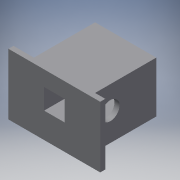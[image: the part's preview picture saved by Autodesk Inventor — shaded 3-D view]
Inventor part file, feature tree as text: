
AUTODESK INVENTOR PART (.ipt)
format: ipt  version: 2016 (Build 200138000, 138)  size: 137,728 bytes
history: native  units: mm
features: extrude x5, sketch x5
ambient origin geometry x8: Origin, YZ Plane, XZ Plane, XY Plane, X Axis, Y Axis, Z Axis, Center Point
bodies: Solid1 (feature_tree)
feature tree (10):
  extrude  "Extrusion1"  Depth=10.0mm
  extrude  "Extrusion2"  Depth=13.0mm
  extrude  "Extrusion3"  Depth=4.0mm
  extrude  "Extrusion4"  Depth=13.0mm TaperAngle=0.0deg
  extrude  "Extrusion5"  Depth=1.0mm
  sketch  "Sketch1"  dims[d0=12.0mm d1=10.0mm]
  sketch  "Sketch2"  dims[d2=13.0mm d3=0.0mm d4=3.6mm]
  sketch  "Sketch3"  dims[d5=4.0mm d7=5.5mm]
  sketch  "Sketch4"  dims[d8=4.5mm d9=13.0mm d10=0.0mm]
  sketch  "Sketch5"  dims[d11=1.0mm d12=1.0mm d14=1.0mm d15=1.0mm d16=13.0mm d17=0.0mm d18=3.0mm d19=3.0mm d20=1.0mm d21=1.0mm d22=1.0mm d23=0.0mm d27=2.0mm d28=4.0mm d29=4.0mm d30=3.0mm d31=9.0mm d32=1.0mm d33=0.0mm d34=18.0mm d35=12.0mm d36=12.0mm]
